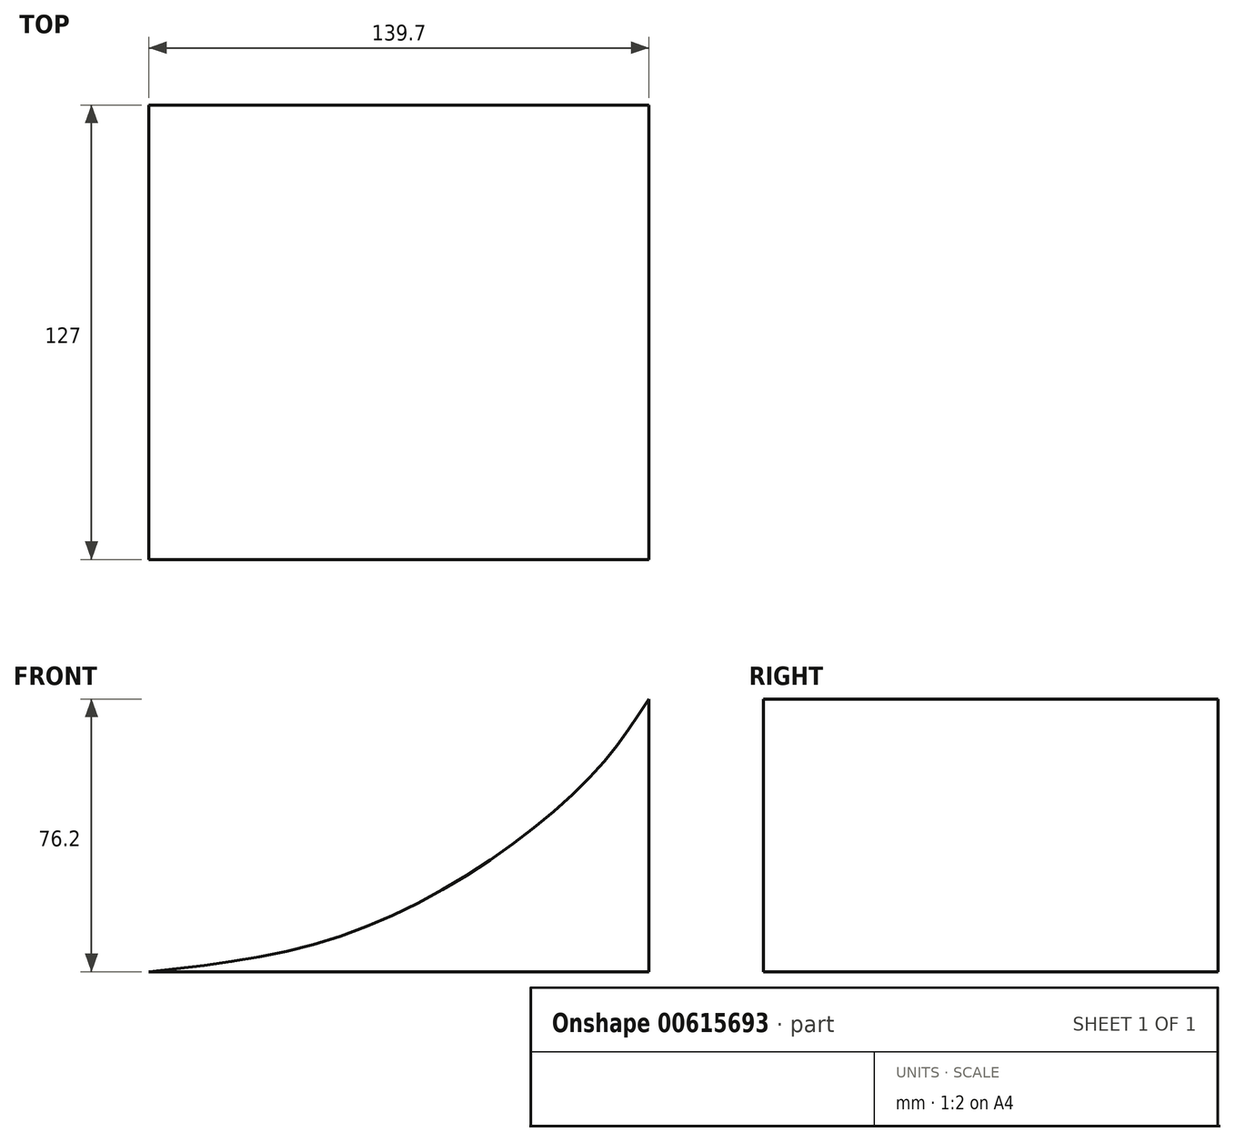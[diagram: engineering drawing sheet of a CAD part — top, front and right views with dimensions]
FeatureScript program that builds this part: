
annotation { "Feature Type Name" : "Feature", "Feature Type Description" : "" }
export const myFeature = defineFeature(function(context is Context, id is Id, definition is map)
    precondition{}
    {
        {
            var Q0;
            Q0=qCreatedBy(makeId("Front.planeOp"),FACE);
            var sketch = newSketch(context, id + "F0", { "sketchPlane" : qUnion([Q0])});
            skLineSegment(sketch, "E0", {"start": v(-71.58, 0) * mm, "end": v(68.12, 0) * mm});
            skLineSegment(sketch, "E1", {"start": v(68.12, 0) * mm, "end": v(68.12, 76.2) * mm});
            skPoint(sketch, "E2", {"position": v(53.9, 56.79) * mm});
            skPoint(sketch, "E3", {"position": v(22.04, 30) * mm});
            skPoint(sketch, "E4", {"position": v(-23.05, 8.3) * mm});
            skPoint(sketch, "E5", {"position": v(-71.58, 0) * mm});
            skFitSpline(sketch, "E6", {"points": [v(68.12, 76.2) * mm, v(53.9, 56.79) * mm, v(22.04, 30) * mm, v(-23.05, 8.3) * mm, v(-71.58, 0) * mm], "startDerivative": vector(-63.63, -98.64) * mm, "endDerivative": vector(-178.04, -19.47) * mm});
            skSolve(sketch);
        }
        {
            var Q0;
            Q0=makeQuery(id+"F0.imprint","IMPRINT",FACE,{"disambiguationData":[TD([[makeQuery(id+"F0.imprint","IMPRINT",EDGE,{"derivedFrom":sQuery(id+"F0.wireOp",EDGE,"E0")}),1.0]])]});
            extrude(context, id + "F1", {"entities" : qUnion([Q0]), "depth" : 127 * mm, "offsetDistance" : 25.4 * mm});
        }
    });
